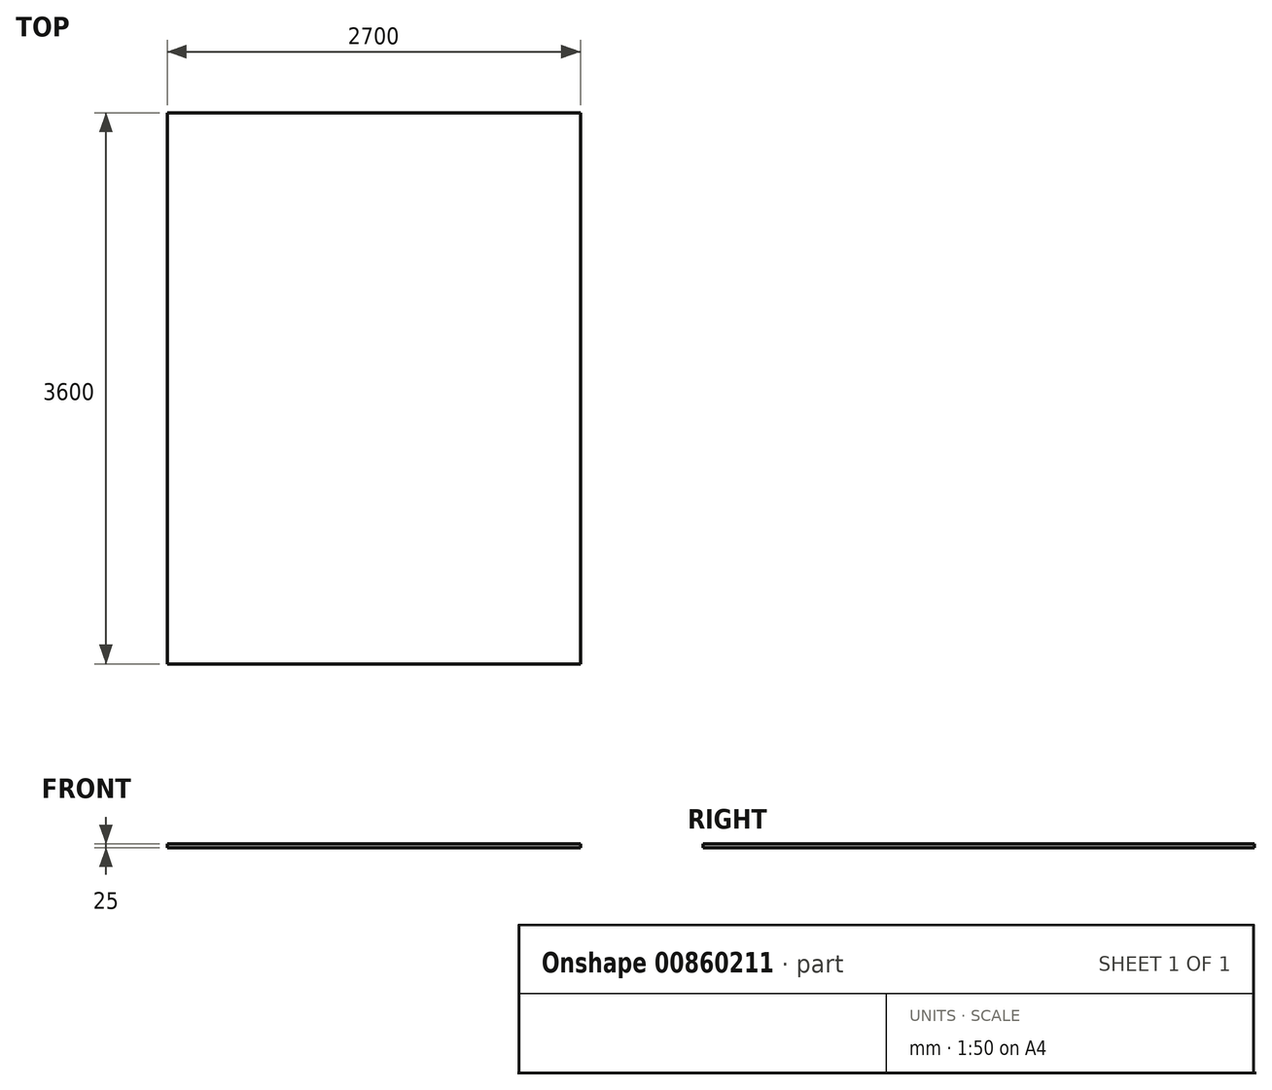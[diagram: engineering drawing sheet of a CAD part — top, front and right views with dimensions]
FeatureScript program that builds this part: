
annotation { "Feature Type Name" : "Feature", "Feature Type Description" : "" }
export const myFeature = defineFeature(function(context is Context, id is Id, definition is map)
    precondition{}
    {
        {
            var Q0;
            Q0=qCreatedBy(makeId("Top.planeOp"),FACE);
            var sketch = newSketch(context, id + "F0", { "sketchPlane" : qUnion([Q0])});
            skLineSegment(sketch, "E0.bottom", {"start": v(0, 0) * mm, "end": v(2700, 0) * mm});
            skLineSegment(sketch, "E0.top", {"start": v(0, 3600) * mm, "end": v(2700, 3600) * mm});
            skLineSegment(sketch, "E0.left", {"start": v(0, 0) * mm, "end": v(0, 3600) * mm});
            skLineSegment(sketch, "E0.right", {"start": v(2700, 0) * mm, "end": v(2700, 3600) * mm});
            skSolve(sketch);
        }
        {
            var Q0;
            Q0 = qSketchRegion(id + "F0", true);
            extrude(context, id + "F1", {"entities" : qUnion([Q0]), "depth" : 25 * mm, "offsetDistance" : 25 * mm});
        }
    });
